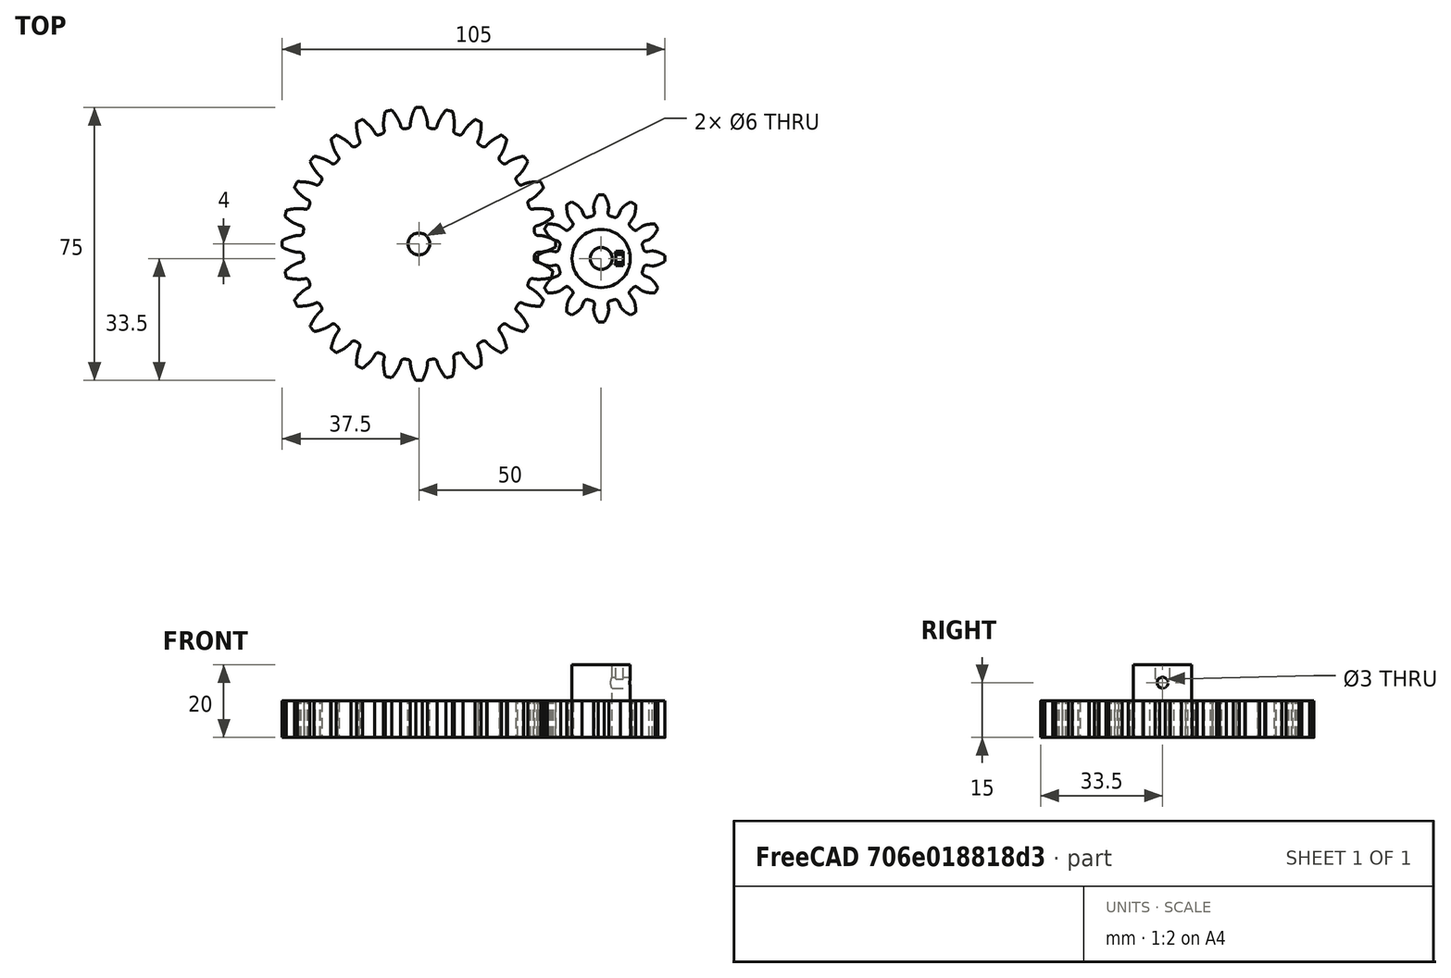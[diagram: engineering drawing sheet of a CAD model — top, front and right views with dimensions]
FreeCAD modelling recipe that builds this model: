
FCSTD DOCUMENT  (FreeCAD 0.18R4 (GitTag))
Label: engranajes
License: All rights reserved
LicenseURL: http://en.wikipedia.org/wiki/All_rights_reserved
objects: Part::Cylinder×5, Part::Cut×4, Part::Part2DObjectPython×2, Part::Extrusion×2, Part::MultiFuse×1, Part::Box×1
note: 15 computed .brp shape members not serialized (recipe doc carries the construction recipe); baked Part::Feature solids carry a one-line shape summary decoded from their .brp

FEATURE [Part::Part2DObjectPython] InvoluteGear  # Draft 2D object (typed FeaturePython)
  ExternalGear = true
  HighPrecision = true
  Modules = 2.5
  NumberOfTeeth = 28
  PressureAngle = 20
FEATURE [Part::Extrusion] Extrude
  Base = -> InvoluteGear
  Dir = (0,0,1)
  DirMode = 2
  FaceMakerClass = Part::FaceMakerBullseye
  LengthFwd = 10
  LengthRev = 0
  Solid = true
  Symmetric = false
FEATURE [Part::Part2DObjectPython] InvoluteGear001  # Draft 2D object (typed FeaturePython)
  ExternalGear = true
  HighPrecision = true
  Modules = 2.5
  NumberOfTeeth = 12
  PressureAngle = 20
FEATURE [Part::Extrusion] Extrude001
  Base = -> InvoluteGear001
  Dir = (0,0,1)
  DirMode = 2
  FaceMakerClass = Part::FaceMakerBullseye
  LengthFwd = 10
  LengthRev = 0
  Placement = pos=(50,-4,0) rot=(0,0,1;0rad)
  Solid = true
  Symmetric = false
FEATURE [Part::Cylinder] Cylinder  label="Cilindro"
  Angle = 360
  AttacherType = Attacher::AttachEngine3D
  Height = 20
  Placement = pos=(50,-4,0) rot=(0,0,1;0rad)
  Radius = 8
FEATURE [Part::Cylinder] Cylinder001  label="Cilindro001"
  Angle = 360
  AttacherType = Attacher::AttachEngine3D
  Height = 10
  Placement = pos=(50,-4,0) rot=(0,0,1;0rad)
  Radius = 8
FEATURE [Part::Cylinder] Cylinder002  label="Cilindro002"
  Angle = 360
  AttacherType = Attacher::AttachEngine3D
  Height = 20
  Placement = pos=(50,-4,0) rot=(0,0,1;0rad)
  Radius = 3
FEATURE [Part::MultiFuse] Fusion
  Shapes = -> [Extrude001,Cylinder]
FEATURE [Part::Cut] Cut
  Base = -> Fusion
  Tool = -> Cylinder002
FEATURE [Part::Box] Box  label="Cubo"
  AttacherType = Attacher::AttachEngine3D
  Height = 4
  Length = 2
  Placement = pos=(54,-6,16) rot=(0,0,1;0rad)
  Width = 4
FEATURE [Part::Cut] Cut001
  Base = -> Cut
  Tool = -> Box
FEATURE [Part::Cylinder] Cylinder003  label="Cilindro003"
  Angle = 360
  AttacherType = Attacher::AttachEngine3D
  Height = 10
  Radius = 3
FEATURE [Part::Cylinder] Cylinder004  label="Cilindro004"
  Angle = 360
  AttacherType = Attacher::AttachEngine3D
  Height = 10
  Placement = pos=(51,-4,15) rot=(0,1,0;1.5708rad)
  Radius = 1.5
FEATURE [Part::Cut] Cut002
  Base = -> Extrude
  Tool = -> Cylinder003
FEATURE [Part::Cut] Cut003
  Base = -> Cut001
  Tool = -> Cylinder004
